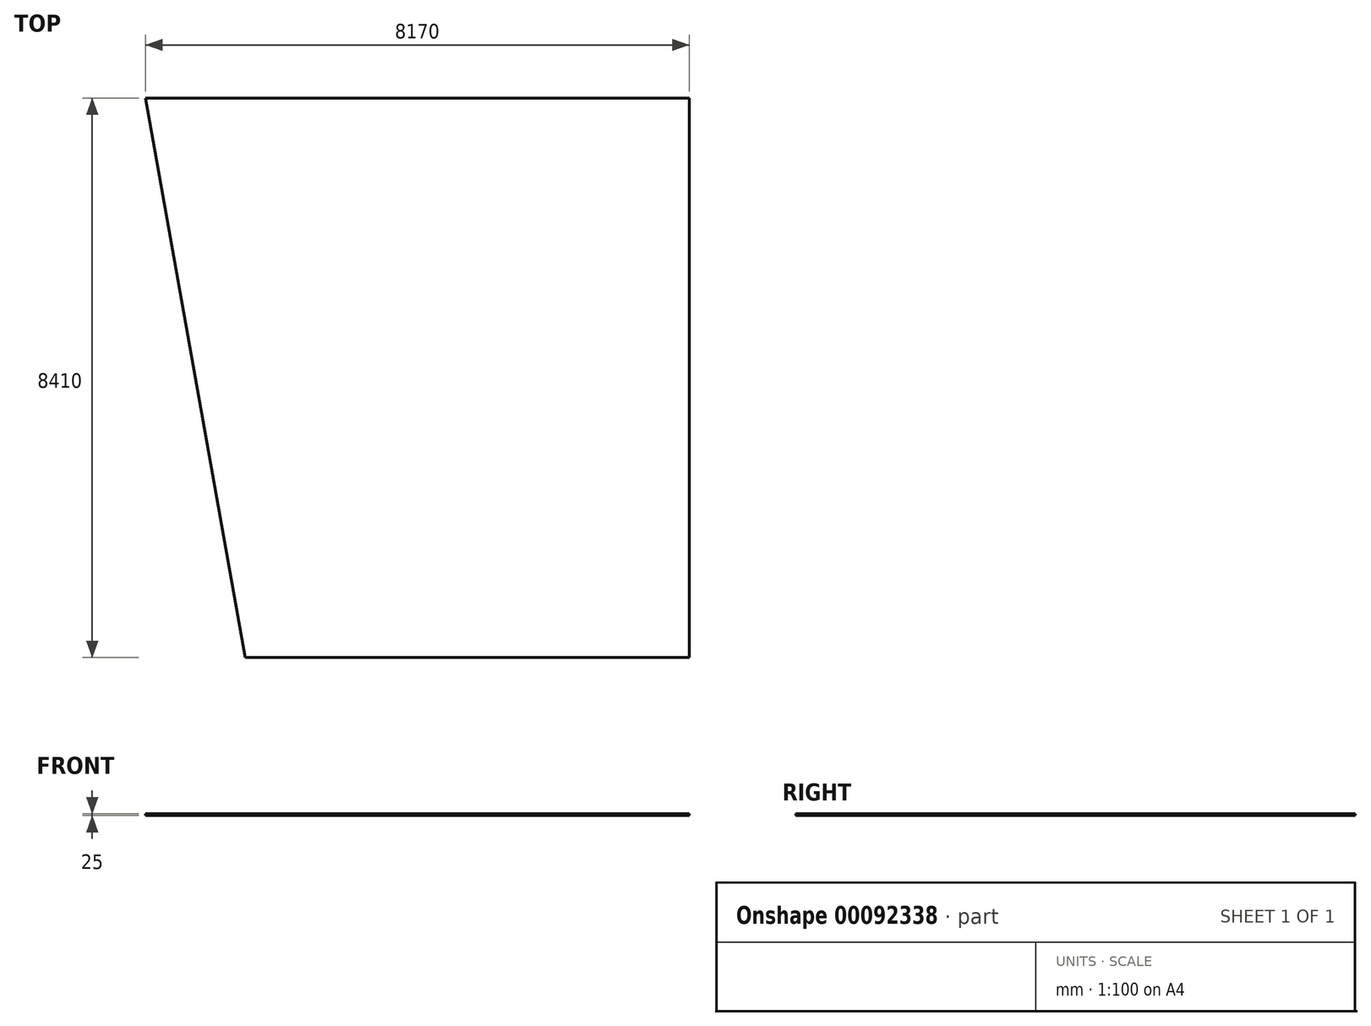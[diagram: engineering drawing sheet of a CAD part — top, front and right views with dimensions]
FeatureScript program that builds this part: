
annotation { "Feature Type Name" : "Feature", "Feature Type Description" : "" }
export const myFeature = defineFeature(function(context is Context, id is Id, definition is map)
    precondition{}
    {
        {
            var Q0;
            Q0=qCreatedBy(makeId("Top.planeOp"),FACE);
            var sketch = newSketch(context, id + "F0", { "sketchPlane" : qUnion([Q0])});
            skLineSegment(sketch, "E0", {"start": v(0, 0) * mm, "end": v(0, 8410) * mm});
            skLineSegment(sketch, "E1", {"start": v(0, 8410) * mm, "end": v(-8170, 8410) * mm});
            skLineSegment(sketch, "E2", {"start": v(-8170, 8410) * mm, "end": v(-6670.13, 0) * mm});
            skLineSegment(sketch, "E3", {"start": v(-6670.13, 0) * mm, "end": v(0, 0) * mm});
            skSolve(sketch);
        }
        {
            var Q0;
            Q0=makeQuery(id+"F0.imprint","IMPRINT",FACE,{"disambiguationData":[TD([[makeQuery(id+"F0.imprint","IMPRINT",EDGE,{"derivedFrom":sQuery(id+"F0.wireOp",EDGE,"E0")}),1.0]])]});
            extrude(context, id + "F1", {"entities" : qUnion([Q0]), "depth" : 25 * mm, "offsetDistance" : 25 * mm});
        }
    });
